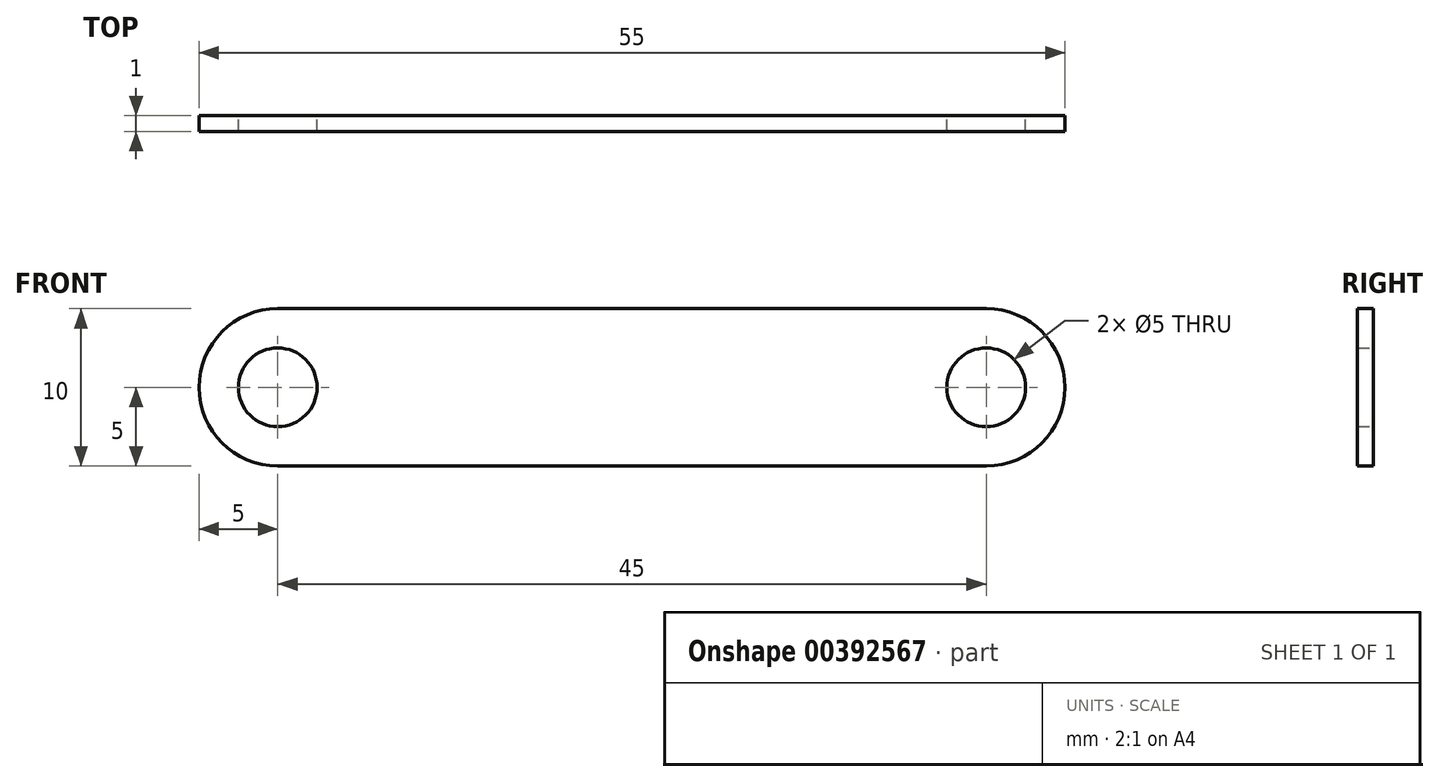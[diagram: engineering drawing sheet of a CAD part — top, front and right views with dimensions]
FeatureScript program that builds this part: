
annotation { "Feature Type Name" : "Feature", "Feature Type Description" : "" }
export const myFeature = defineFeature(function(context is Context, id is Id, definition is map)
    precondition{}
    {
        {
            var Q0;
            Q0=qCreatedBy(makeId("Front.planeOp"),FACE);
            var sketch = newSketch(context, id + "F0", { "sketchPlane" : qUnion([Q0])});
            skLineSegment(sketch, "E0", {"start": v(0, 0) * mm, "end": v(45, 0) * mm, "construction": true});
            skArc(sketch, "E1", {"start": v(45, -5) * mm, "mid": v(50, 0) * mm, "end": v(45, 5) * mm});
            skArc(sketch, "E2", {"start": v(0, 5) * mm, "mid": v(-5, 0) * mm, "end": v(0, -5) * mm});
            skLineSegment(sketch, "E3", {"start": v(0, 5) * mm, "end": v(45, 5) * mm});
            skLineSegment(sketch, "E4", {"start": v(0, -5) * mm, "end": v(45, -5) * mm});
            skCircle(sketch, "E5", {"center": v(0, 0) * mm, "radius": 2.5 * mm});
            skCircle(sketch, "E6", {"center": v(45, 0) * mm, "radius": 2.5 * mm});
            skSolve(sketch);
        }
        {
            var Q0;
            Q0=makeQuery(id+"F0.imprint","IMPRINT",FACE,{"disambiguationData":[TD([[makeQuery(id+"F0.imprint","IMPRINT",EDGE,{"derivedFrom":sQuery(id+"F0.wireOp",EDGE,"E1")}),1.0]])]});
            extrude(context, id + "F1", {"entities" : qUnion([Q0]), "endBound" : BoundingType.SYMMETRIC, "depth" : 1 * mm});
        }
    });
